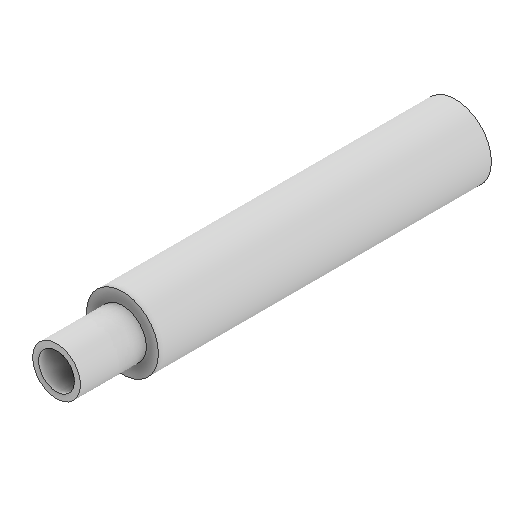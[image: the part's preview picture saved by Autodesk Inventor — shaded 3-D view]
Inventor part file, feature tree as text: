
AUTODESK INVENTOR PART (.ipt)
format: ipt  version: 2025.1 (Build 291241000, 241)  size: 104,448 bytes
history: native  units: mm
features: extrude x2, other x1, sketch x1
ambient origin geometry x8: Origin, YZ Plane, XZ Plane, XY Plane, X Axis, Y Axis, Z Axis, Center Point
bodies: Body1 (feature_tree)
feature tree (4):
  other  "Bryła1"
  sketch  "Szkic1"
  extrude  "Wyciągnięcie proste1"  Depth=3.0mm
  extrude  "Wyciągnięcie proste2"  Depth=4.0mm
